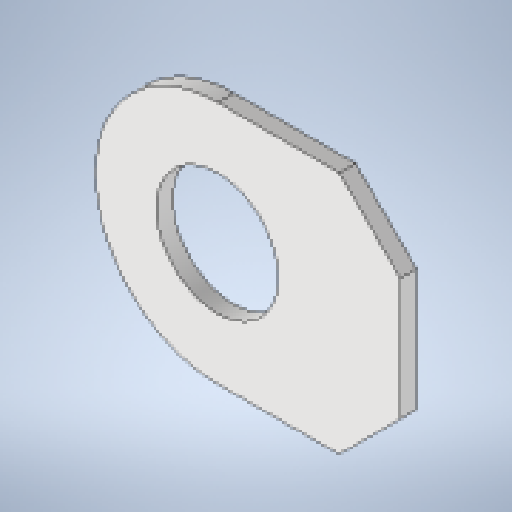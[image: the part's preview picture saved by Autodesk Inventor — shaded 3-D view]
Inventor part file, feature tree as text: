
AUTODESK INVENTOR PART (.ipt)
format: ipt  version: 2025.1 (Build 291241020, 241B)  size: 174,080 bytes
history: native  units: mm
features: other x2, sheet_metal_op x1, sketch x1
ambient origin geometry x8: Origin, YZ Plane, XZ Plane, XY Plane, X Axis, Y Axis, Z Axis, Center Point
bodies: Solid1 (feature_tree)
feature tree (4):
  sheet_metal_op  "Face1"
  sketch  "Sketch1"  dims[d0=170.0mm d1=120.0mm d2=8.0mm d13=60.0mm d14=60.0mm d15=30.0mm d17=45.0deg]
  other  "Plate1"
  other  "Definition1"
